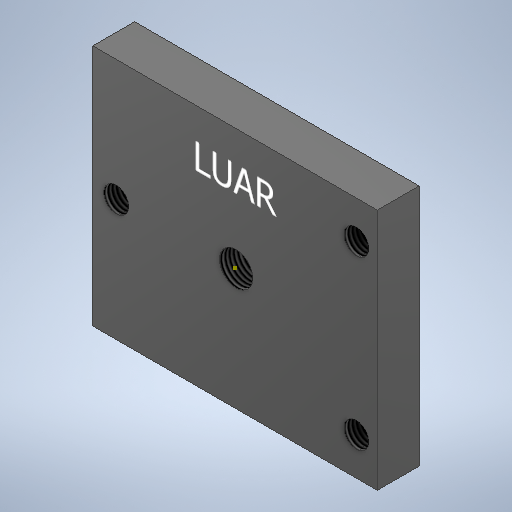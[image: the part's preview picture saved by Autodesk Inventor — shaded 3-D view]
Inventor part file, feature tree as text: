
AUTODESK INVENTOR PART (.ipt)
format: ipt  version: 2025.1 (Build 291241000, 241)  size: 269,312 bytes
history: native  units: mm
features: sketch x4, thread x4, extrude x2
ambient origin geometry x8: Origin, YZ Plane, XZ Plane, XY Plane, X Axis, Y Axis, Z Axis, Center Point
bodies: Solid1 (feature_tree)
feature tree (10):
  sketch  "Sketch1"  dims[d0=34.0mm d1=29.0mm d2=3.0mm d3=3.0mm d4=3.0mm]
  extrude  "Extrusion1"  Depth=29.0mm
  thread  "Thread1"  [1 undecoded]
  thread  "Thread2"  [1 undecoded]
  thread  "Thread3"  [1 undecoded]
  sketch  "Sketch3"  dims[d8=28.7mm]
  extrude  "Extrusion2"  Depth=2.5mm
  thread  "Thread4"  [1 undecoded]
  sketch  "Sketch2"  dims[d5=20.0mm d6=2.5mm d7=14.5mm]
  sketch  "Sketch4"  dims[d10=5.0mm d11=0.0mm d12=5.0mm d13=0.0mm d14=5.0mm d15=0.0mm d16=5.0mm d17=0.0mm d18=4.0mm d21=14.375mm d22=5.0mm d23=0.0mm d24=5.0mm d25=0.0mm]
note: 4 required parameter values undecoded (feature->parameter linkage not recoverable at this tier; creation-order binding heuristic only, values carry confidence <= 0.55)
